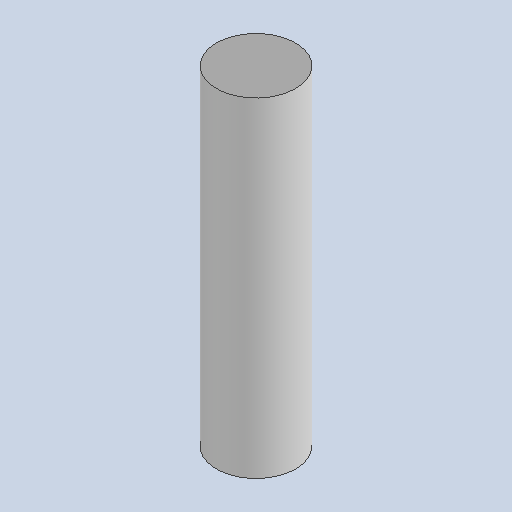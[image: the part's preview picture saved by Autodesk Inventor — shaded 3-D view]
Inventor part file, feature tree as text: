
AUTODESK INVENTOR PART (.ipt)
format: ipt  version: 2025 (Build 290162010, 162A)  size: 79,872 bytes
history: native  units: mm
features: extrude x1, sketch x1
ambient origin geometry x8: Origin, YZ Plane, XZ Plane, XY Plane, X Axis, Y Axis, Z Axis, Center Point
bodies: Solid1 (feature_tree)
feature tree (2):
  extrude  "Extrusion1"  Depth=50.0mm TaperAngle=0.0deg
  sketch  "Sketch1"  dims[d0=12.0mm d1=50.0mm d2=40.0mm d3=0.0mm d4=0.0mm]
